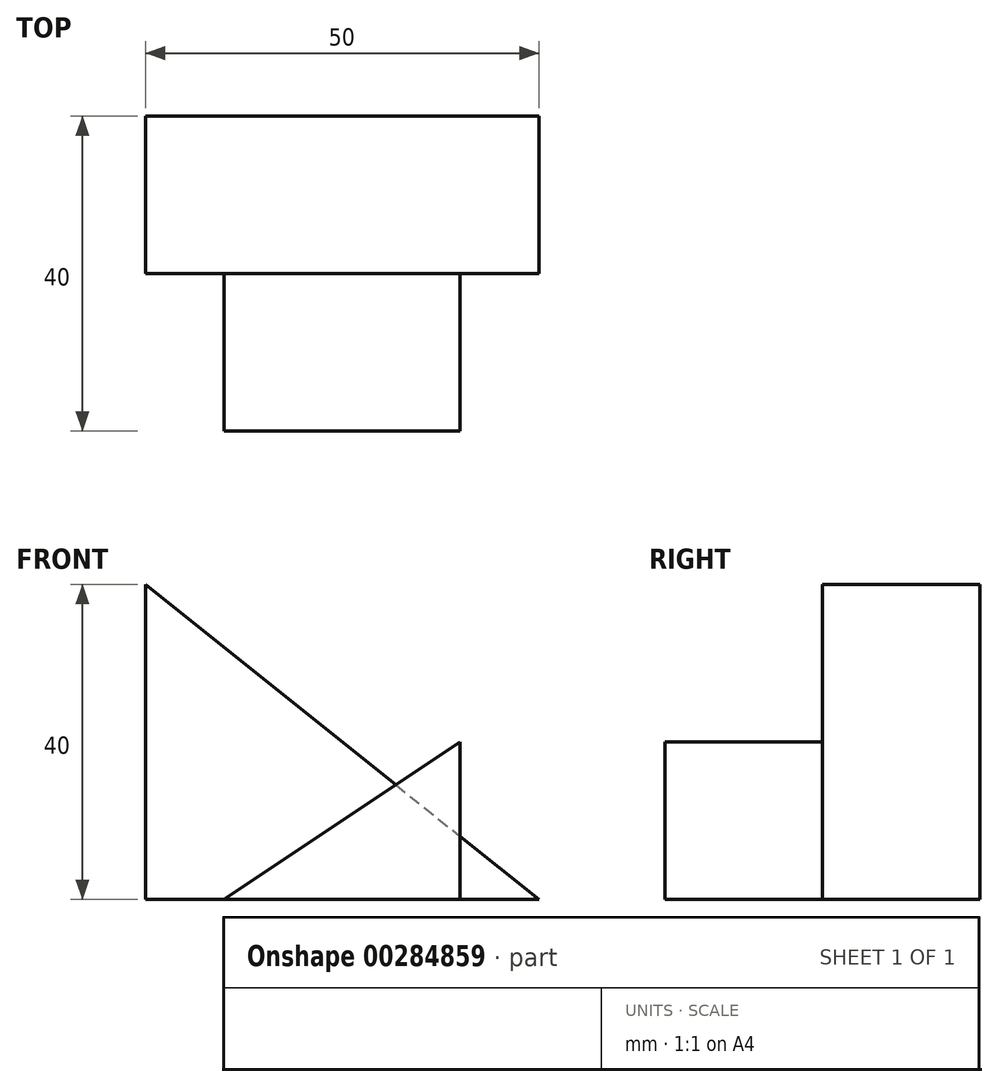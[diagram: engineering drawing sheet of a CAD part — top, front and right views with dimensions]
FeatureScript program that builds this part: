
annotation { "Feature Type Name" : "Feature", "Feature Type Description" : "" }
export const myFeature = defineFeature(function(context is Context, id is Id, definition is map)
    precondition{}
    {
        {
            var Q0;
            Q0=qCreatedBy(makeId("Front.planeOp"),FACE);
            var sketch = newSketch(context, id + "F0", { "sketchPlane" : qUnion([Q0])});
            skLineSegment(sketch, "E0.bottom", {"start": v(0, 0) * mm, "end": v(50, 0) * mm});
            skLineSegment(sketch, "E0.top", {"start": v(0, 40) * mm, "end": v(50, 40) * mm});
            skLineSegment(sketch, "E0.left", {"start": v(0, 0) * mm, "end": v(0, 40) * mm});
            skLineSegment(sketch, "E0.right", {"start": v(50, 0) * mm, "end": v(50, 40) * mm});
            skLineSegment(sketch, "E1", {"start": v(0, 40) * mm, "end": v(50, 0) * mm});
            skSolve(sketch);
        }
        {
            var Q0;
            Q0=makeQuery(id+"F0.imprint","IMPRINT",FACE,{"disambiguationData":[TD([[makeQuery(id+"F0.imprint","IMPRINT",EDGE,{"derivedFrom":sQuery(id+"F0.wireOp",EDGE,"E0.bottom")}),1.0]])]});
            extrude(context, id + "F1", {"entities" : qUnion([Q0]), "depth" : 20 * mm});
        }
        {
            var Q0;
            Q0=makeQuery(id+"F1.opExtrude","CAP_FACE",FACE,{"disambiguationData":[OSD([sQuery(id+"F0.wireOp",EDGE,"E0.bottom"),sQuery(id+"F0.wireOp",EDGE,"E0.top"),sQuery(id+"F0.wireOp",EDGE,"E0.left"),sQuery(id+"F0.wireOp",EDGE,"E0.right")])],"isStart":false});
            var sketch = newSketch(context, id + "F2", { "sketchPlane" : qUnion([Q0])});
            skLineSegment(sketch, "E2.bottom", {"start": v(10, 0) * mm, "end": v(40, 0) * mm});
            skLineSegment(sketch, "E2.top", {"start": v(10, 20) * mm, "end": v(40, 20) * mm});
            skLineSegment(sketch, "E2.left", {"start": v(10, 0) * mm, "end": v(10, 20) * mm});
            skLineSegment(sketch, "E2.right", {"start": v(40, 0) * mm, "end": v(40, 20) * mm});
            skLineSegment(sketch, "E3", {"start": v(40, 20) * mm, "end": v(10, 0) * mm});
            skSolve(sketch);
        }
        {
            var Q0;
            Q0=makeQuery(id+"F2.imprint","IMPRINT",FACE,{"disambiguationData":[TD([[makeQuery(id+"F2.imprint","IMPRINT",EDGE,{"derivedFrom":sQuery(id+"F2.wireOp",EDGE,"E2.bottom")}),1.0]])]});
            var Q1;
            {var subQ1=sQuery(id+"F2.wireOp",EDGE,"E2.right");var subQ3=makeQuery(id+"F1.opExtrude","CAP_EDGE",EDGE,{"disambiguationData":[OSD([sQuery(id+"F0.wireOp",EDGE,"E1")])],"isStart":false});var subQ4=makeQuery(id+"F2.imprint","INTERSECT",VERTEX,{"derivedFrom":[subQ3,subQ1]});Q1=makeQuery(id+"F2.imprint","IMPRINT",FACE,{"disambiguationData":[TD([[makeQuery(id+"F2.imprint","IMPRINT",EDGE,{"disambiguationData":[TD([[subQ4,1.0]])],"derivedFrom":subQ3}),1.0]])]});}
            extrude(context, id + "F3", {"entities" : qUnion([Q0, Q1]), "operationType" : NewBodyOperationType.ADD, "depth" : 20 * mm});
        }
    });
